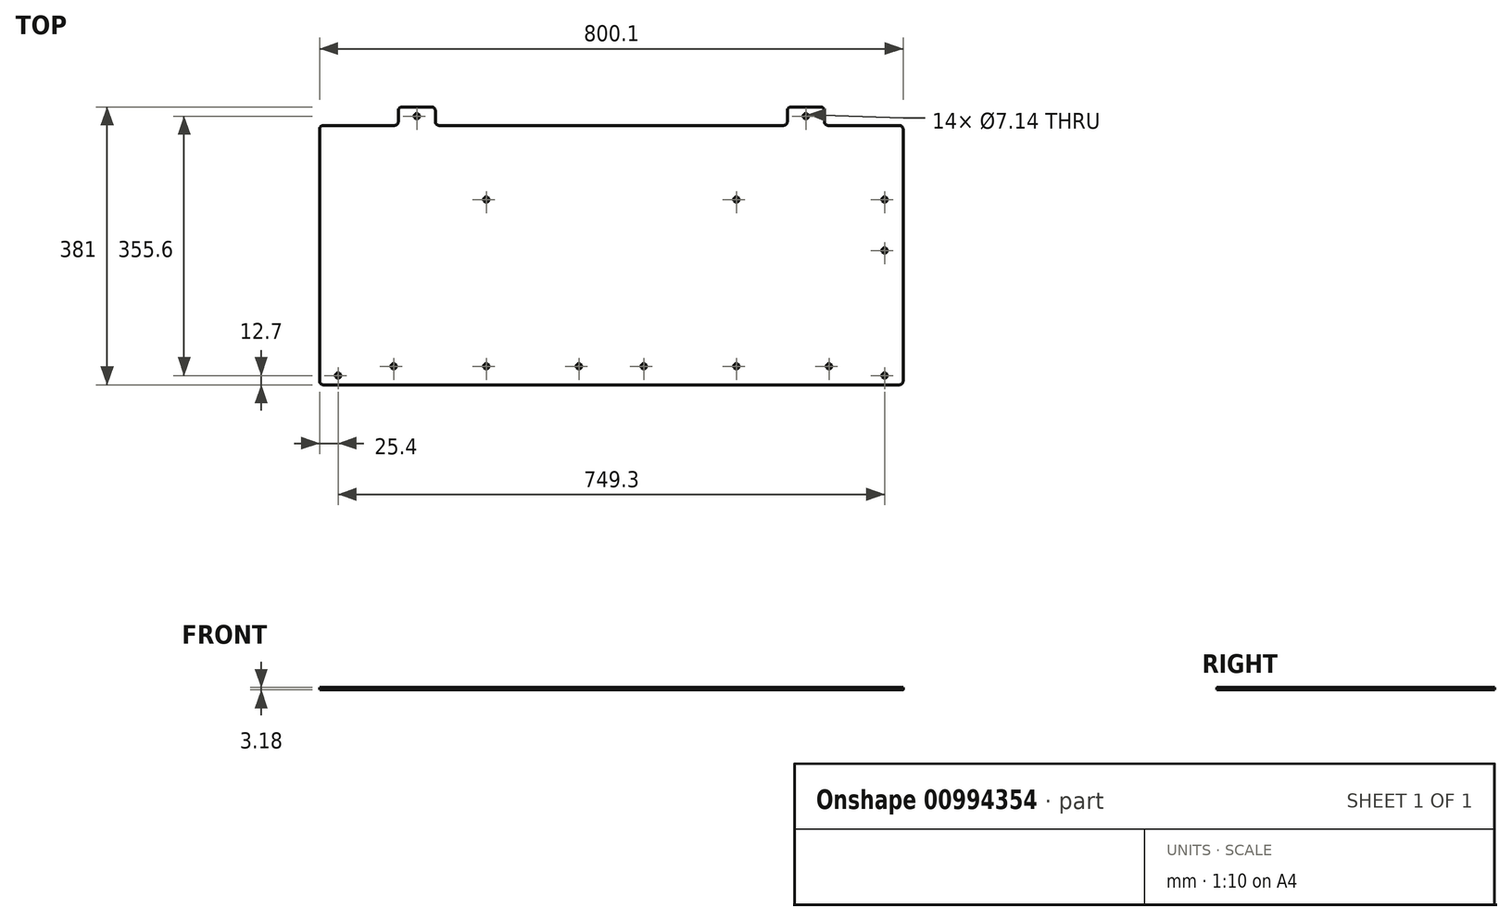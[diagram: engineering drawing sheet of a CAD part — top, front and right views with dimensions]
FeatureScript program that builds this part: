
annotation { "Feature Type Name" : "Feature", "Feature Type Description" : "" }
export const myFeature = defineFeature(function(context is Context, id is Id, definition is map)
    precondition{}
    {
        {
            var Q0;
            Q0=qCreatedBy(makeId("Top.planeOp"),FACE);
            var sketch = newSketch(context, id + "F0", { "sketchPlane" : qUnion([Q0])});
            skLineSegment(sketch, "E0.bottom", {"start": v(0, 0) * mm, "end": v(800.1, 0) * mm});
            skLineSegment(sketch, "E0.top", {"start": v(0, 355.6) * mm, "end": v(800.1, 355.6) * mm});
            skLineSegment(sketch, "E0.left", {"start": v(0, 0) * mm, "end": v(0, 355.6) * mm});
            skLineSegment(sketch, "E0.right", {"start": v(800.1, 0) * mm, "end": v(800.1, 355.6) * mm});
            skLineSegment(sketch, "E1", {"start": v(400.05, 355.6) * mm, "end": v(400.05, 0) * mm});
            skLineSegment(sketch, "E2", {"start": v(107.95, 355.6) * mm, "end": v(107.95, 0) * mm});
            skLineSegment(sketch, "E3", {"start": v(692.15, 355.6) * mm, "end": v(692.15, 0) * mm});
            skLineSegment(sketch, "E4.bottom", {"start": v(107.95, 355.6) * mm, "end": v(158.75, 355.6) * mm});
            skLineSegment(sketch, "E4.top", {"start": v(107.95, 381) * mm, "end": v(158.75, 381) * mm});
            skLineSegment(sketch, "E4.left", {"start": v(107.95, 355.6) * mm, "end": v(107.95, 381) * mm});
            skLineSegment(sketch, "E4.right", {"start": v(158.75, 355.6) * mm, "end": v(158.75, 381) * mm});
            skLineSegment(sketch, "E5.MirrorCS", {"start": v(641.35, 355.6) * mm, "end": v(641.35, 381) * mm});
            skLineSegment(sketch, "E6.MirrorCS", {"start": v(692.15, 381) * mm, "end": v(641.35, 381) * mm});
            skLineSegment(sketch, "E7.MirrorCS", {"start": v(692.15, 355.6) * mm, "end": v(692.15, 381) * mm});
            skPoint(sketch, "E8", {"position": v(133.35, 368.3) * mm});
            skPoint(sketch, "E9.MirrorP", {"position": v(666.75, 368.3) * mm});
            skPoint(sketch, "E10", {"position": v(25.4, 12.7) * mm});
            skPoint(sketch, "E11.MirrorP", {"position": v(774.7, 12.7) * mm});
            skSolve(sketch);
        }
        {
            var Q0;
            {var subQ2=sQuery(id+"F0.wireOp",EDGE,"E0.left");Q0=makeQuery(id+"F0.imprint","IMPRINT",FACE,{"disambiguationData":[TD([[makeQuery(id+"F0.imprint","IMPRINT",EDGE,{"derivedFrom":subQ2}),-1.0]])]});}
            var Q1;
            {var subQ0=sQuery(id+"F0.wireOp",EDGE,"E1");Q1=makeQuery(id+"F0.imprint","IMPRINT",FACE,{"disambiguationData":[TD([[makeQuery(id+"F0.imprint","IMPRINT",EDGE,{"derivedFrom":subQ0}),-1.0]])]});}
            var Q2;
            Q2=makeQuery(id+"F0.imprint","IMPRINT",FACE,{"disambiguationData":[TD([[makeQuery(id+"F0.imprint","IMPRINT",EDGE,{"derivedFrom":sQuery(id+"F0.wireOp",EDGE,"E4.top")}),-1.0]])]});
            var Q3;
            {var subQ0=sQuery(id+"F0.wireOp",EDGE,"E1");Q3=makeQuery(id+"F0.imprint","IMPRINT",FACE,{"disambiguationData":[TD([[makeQuery(id+"F0.imprint","IMPRINT",EDGE,{"derivedFrom":subQ0}),1.0]])]});}
            var Q4;
            {var subQ0=sQuery(id+"F0.wireOp",EDGE,"E0.right");Q4=makeQuery(id+"F0.imprint","IMPRINT",FACE,{"disambiguationData":[TD([[makeQuery(id+"F0.imprint","IMPRINT",EDGE,{"derivedFrom":subQ0}),1.0]])]});}
            var Q5;
            {var subQ2=sQuery(id+"F0.wireOp",EDGE,"E5.MirrorCS");Q5=makeQuery(id+"F0.imprint","IMPRINT",FACE,{"disambiguationData":[TD([[makeQuery(id+"F0.imprint","IMPRINT",EDGE,{"derivedFrom":subQ2}),-1.0]])]});}
            extrude(context, id + "F1", {"entities" : qUnion([Q0, Q1, Q2, Q3, Q4, Q5]), "depth" : 3.17 * mm, "offsetDistance" : 25.4 * mm});
        }
        {
            var Q0;
            Q0=sQuery(id+"F0.wireOp",VERTEX,"E8");
            var Q1;
            Q1=sQuery(id+"F0.wireOp",VERTEX,"E9.MirrorP");
            var Q2;
            Q2=sQuery(id+"F0.wireOp",VERTEX,"E10");
            var Q3;
            Q3=sQuery(id+"F0.wireOp",VERTEX,"E11.MirrorP");
            var Q4;
            Q4=makeQuery(id+"F1.opExtrude","SWEPT_BODY",BODY,{"disambiguationData":[OSD([sQuery(id+"F0.wireOp",EDGE,"E0.bottom"),sQuery(id+"F0.wireOp",EDGE,"E0.top"),sQuery(id+"F0.wireOp",EDGE,"E0.left"),sQuery(id+"F0.wireOp",EDGE,"E0.right"),sQuery(id+"F0.wireOp",EDGE,"E4.top"),sQuery(id+"F0.wireOp",EDGE,"E4.left"),sQuery(id+"F0.wireOp",EDGE,"E4.right"),sQuery(id+"F0.wireOp",EDGE,"E5.MirrorCS"),sQuery(id+"F0.wireOp",EDGE,"E6.MirrorCS"),sQuery(id+"F0.wireOp",EDGE,"E7.MirrorCS")])]});
            hole(context, id + "F2", {"style" : HoleStyle.SIMPLE, "endStyle" : HoleEndStyle.THROUGH, "oppositeDirection" : true, "standardTappedOrClearance" : lookupTablePath({ "fit" : "Normal (ASME)", "standard" : "ANSI", "size" : "1/4", "type" : "Clearance" }), "standardBlindInLast" : lookupTablePath({ "fit" : "Normal", "standard" : "ANSI", "engagement" : "75%", "pitch" : "20 tpi", "size" : "1/4", "type" : "Clearance & tapped" }), "holeDiameter" : 7.14 * mm, "majorDiameter" : 6.35 * mm, "isTappedThrough" : true, "tappedDepth" : 12.7 * mm, "tapClearance" : 3, "locations" : qUnion([Q0, Q1, Q2, Q3]), "scope" : qUnion([Q4])});
        }
        {
            var Q0;
            Q0=makeQuery(id+"F1.opExtrude","SWEPT_EDGE",EDGE,{"disambiguationData":[OSD([sQuery(id+"F0.wireOp",EDGE,"E0.top"),sQuery(id+"F0.wireOp",EDGE,"E0.left")])]});
            var Q1;
            Q1=makeQuery(id+"F1.opExtrude","SWEPT_EDGE",EDGE,{"disambiguationData":[OSD([sQuery(id+"F0.wireOp",EDGE,"E0.top"),sQuery(id+"F0.wireOp",EDGE,"E2"),sQuery(id+"F0.wireOp",EDGE,"E4.left")])]});
            var Q2;
            Q2=makeQuery(id+"F1.opExtrude","SWEPT_EDGE",EDGE,{"disambiguationData":[OSD([sQuery(id+"F0.wireOp",EDGE,"E4.top"),sQuery(id+"F0.wireOp",EDGE,"E4.left")])]});
            var Q3;
            Q3=makeQuery(id+"F1.opExtrude","SWEPT_EDGE",EDGE,{"disambiguationData":[OSD([sQuery(id+"F0.wireOp",EDGE,"E4.top"),sQuery(id+"F0.wireOp",EDGE,"E4.right")])]});
            var Q4;
            Q4=makeQuery(id+"F1.opExtrude","SWEPT_EDGE",EDGE,{"disambiguationData":[OSD([sQuery(id+"F0.wireOp",EDGE,"E0.top"),sQuery(id+"F0.wireOp",EDGE,"E4.right")])]});
            var Q5;
            Q5=makeQuery(id+"F1.opExtrude","SWEPT_EDGE",EDGE,{"disambiguationData":[OSD([sQuery(id+"F0.wireOp",EDGE,"E0.top"),sQuery(id+"F0.wireOp",EDGE,"E3"),sQuery(id+"F0.wireOp",EDGE,"E7.MirrorCS")])]});
            var Q6;
            Q6=makeQuery(id+"F1.opExtrude","SWEPT_EDGE",EDGE,{"disambiguationData":[OSD([sQuery(id+"F0.wireOp",EDGE,"E6.MirrorCS"),sQuery(id+"F0.wireOp",EDGE,"E7.MirrorCS")])]});
            var Q7;
            Q7=makeQuery(id+"F1.opExtrude","SWEPT_EDGE",EDGE,{"disambiguationData":[OSD([sQuery(id+"F0.wireOp",EDGE,"E5.MirrorCS"),sQuery(id+"F0.wireOp",EDGE,"E6.MirrorCS")])]});
            var Q8;
            Q8=makeQuery(id+"F1.opExtrude","SWEPT_EDGE",EDGE,{"disambiguationData":[OSD([sQuery(id+"F0.wireOp",EDGE,"E0.top"),sQuery(id+"F0.wireOp",EDGE,"E5.MirrorCS")])]});
            var Q9;
            Q9=makeQuery(id+"F1.opExtrude","SWEPT_EDGE",EDGE,{"disambiguationData":[OSD([sQuery(id+"F0.wireOp",EDGE,"E0.top"),sQuery(id+"F0.wireOp",EDGE,"E0.right")])]});
            var Q10;
            Q10=makeQuery(id+"F1.opExtrude","SWEPT_EDGE",EDGE,{"disambiguationData":[OSD([sQuery(id+"F0.wireOp",EDGE,"E0.bottom"),sQuery(id+"F0.wireOp",EDGE,"E0.right")])]});
            var Q11;
            Q11=makeQuery(id+"F1.opExtrude","SWEPT_EDGE",EDGE,{"disambiguationData":[OSD([sQuery(id+"F0.wireOp",EDGE,"E0.bottom"),sQuery(id+"F0.wireOp",EDGE,"E0.left")])]});
            fillet(context, id + "F3", {"entities" : qUnion([Q0, Q1, Q2, Q3, Q4, Q5, Q6, Q7, Q8, Q9, Q10, Q11]), "radius" : 5.08 * mm, "tangentPropagation" : true, "allowEdgeOverflow" : false});
        }
        {
            var Q0;
            Q0=makeQuery(id+"F1.opExtrude","CAP_FACE",FACE,{"disambiguationData":[OSD([sQuery(id+"F0.wireOp",EDGE,"E0.bottom"),sQuery(id+"F0.wireOp",EDGE,"E0.top"),sQuery(id+"F0.wireOp",EDGE,"E0.left"),sQuery(id+"F0.wireOp",EDGE,"E0.right"),sQuery(id+"F0.wireOp",EDGE,"E4.top"),sQuery(id+"F0.wireOp",EDGE,"E4.left"),sQuery(id+"F0.wireOp",EDGE,"E4.right"),sQuery(id+"F0.wireOp",EDGE,"E5.MirrorCS"),sQuery(id+"F0.wireOp",EDGE,"E6.MirrorCS"),sQuery(id+"F0.wireOp",EDGE,"E7.MirrorCS")])],"isStart":false});
            var sketch = newSketch(context, id + "F4", { "sketchPlane" : qUnion([Q0])});
            skPoint(sketch, "E12", {"position": v(571.5, 254) * mm});
            skPoint(sketch, "E13", {"position": v(774.7, 254) * mm});
            skPoint(sketch, "E14", {"position": v(774.7, 184.15) * mm});
            skPoint(sketch, "E15", {"position": v(571.5, 25.4) * mm});
            skPoint(sketch, "E16", {"position": v(444.5, 25.4) * mm});
            skPoint(sketch, "E17", {"position": v(698.5, 25.4) * mm});
            skPoint(sketch, "E18.MirrorP", {"position": v(228.6, 254) * mm});
            skPoint(sketch, "E19.MirrorP", {"position": v(355.6, 25.4) * mm});
            skPoint(sketch, "E20.MirrorP", {"position": v(228.6, 25.4) * mm});
            skPoint(sketch, "E21.MirrorP", {"position": v(101.6, 25.4) * mm});
            skSolve(sketch);
        }
        {
            var Q0;
            Q0=sQuery(id+"F4.wireOp",VERTEX,"d5e8b805-a298-4294-8cf4-f2af9e995efc");
            var Q1;
            Q1=sQuery(id+"F4.wireOp",VERTEX,"E12");
            var Q2;
            Q2=sQuery(id+"F4.wireOp",VERTEX,"E13");
            var Q3;
            Q3=sQuery(id+"F4.wireOp",VERTEX,"E16");
            var Q4;
            Q4=sQuery(id+"F4.wireOp",VERTEX,"E15");
            var Q5;
            Q5=sQuery(id+"F4.wireOp",VERTEX,"E17");
            var Q6;
            Q6=sQuery(id+"F4.wireOp",VERTEX,"E14");
            var Q7;
            Q7=sQuery(id+"F4.wireOp",VERTEX,"E21.MirrorP");
            var Q8;
            Q8=sQuery(id+"F4.wireOp",VERTEX,"E20.MirrorP");
            var Q9;
            Q9=sQuery(id+"F4.wireOp",VERTEX,"E19.MirrorP");
            var Q10;
            Q10=sQuery(id+"F4.wireOp",VERTEX,"E18.MirrorP");
            var Q11;
            Q11=makeQuery(id+"F1.opExtrude","SWEPT_BODY",BODY,{"disambiguationData":[OSD([sQuery(id+"F0.wireOp",EDGE,"E0.bottom"),sQuery(id+"F0.wireOp",EDGE,"E0.top"),sQuery(id+"F0.wireOp",EDGE,"E0.left"),sQuery(id+"F0.wireOp",EDGE,"E0.right"),sQuery(id+"F0.wireOp",EDGE,"E4.top"),sQuery(id+"F0.wireOp",EDGE,"E4.left"),sQuery(id+"F0.wireOp",EDGE,"E4.right"),sQuery(id+"F0.wireOp",EDGE,"E5.MirrorCS"),sQuery(id+"F0.wireOp",EDGE,"E6.MirrorCS"),sQuery(id+"F0.wireOp",EDGE,"E7.MirrorCS")])]});
            hole(context, id + "F5", {"style" : HoleStyle.SIMPLE, "endStyle" : HoleEndStyle.THROUGH, "standardTappedOrClearance" : lookupTablePath({ "fit" : "Normal (ASME)", "standard" : "ANSI", "size" : "1/4", "type" : "Clearance" }), "standardBlindInLast" : lookupTablePath({ "fit" : "Normal", "standard" : "ANSI", "engagement" : "75%", "pitch" : "20 tpi", "size" : "1/4", "type" : "Clearance & tapped" }), "holeDiameter" : 7.14 * mm, "majorDiameter" : 6.35 * mm, "isTappedThrough" : true, "tappedDepth" : 12.7 * mm, "tapClearance" : 3, "locations" : qUnion([Q0, Q1, Q2, Q3, Q4, Q5, Q6, Q7, Q8, Q9, Q10]), "scope" : qUnion([Q11])});
        }
    });
